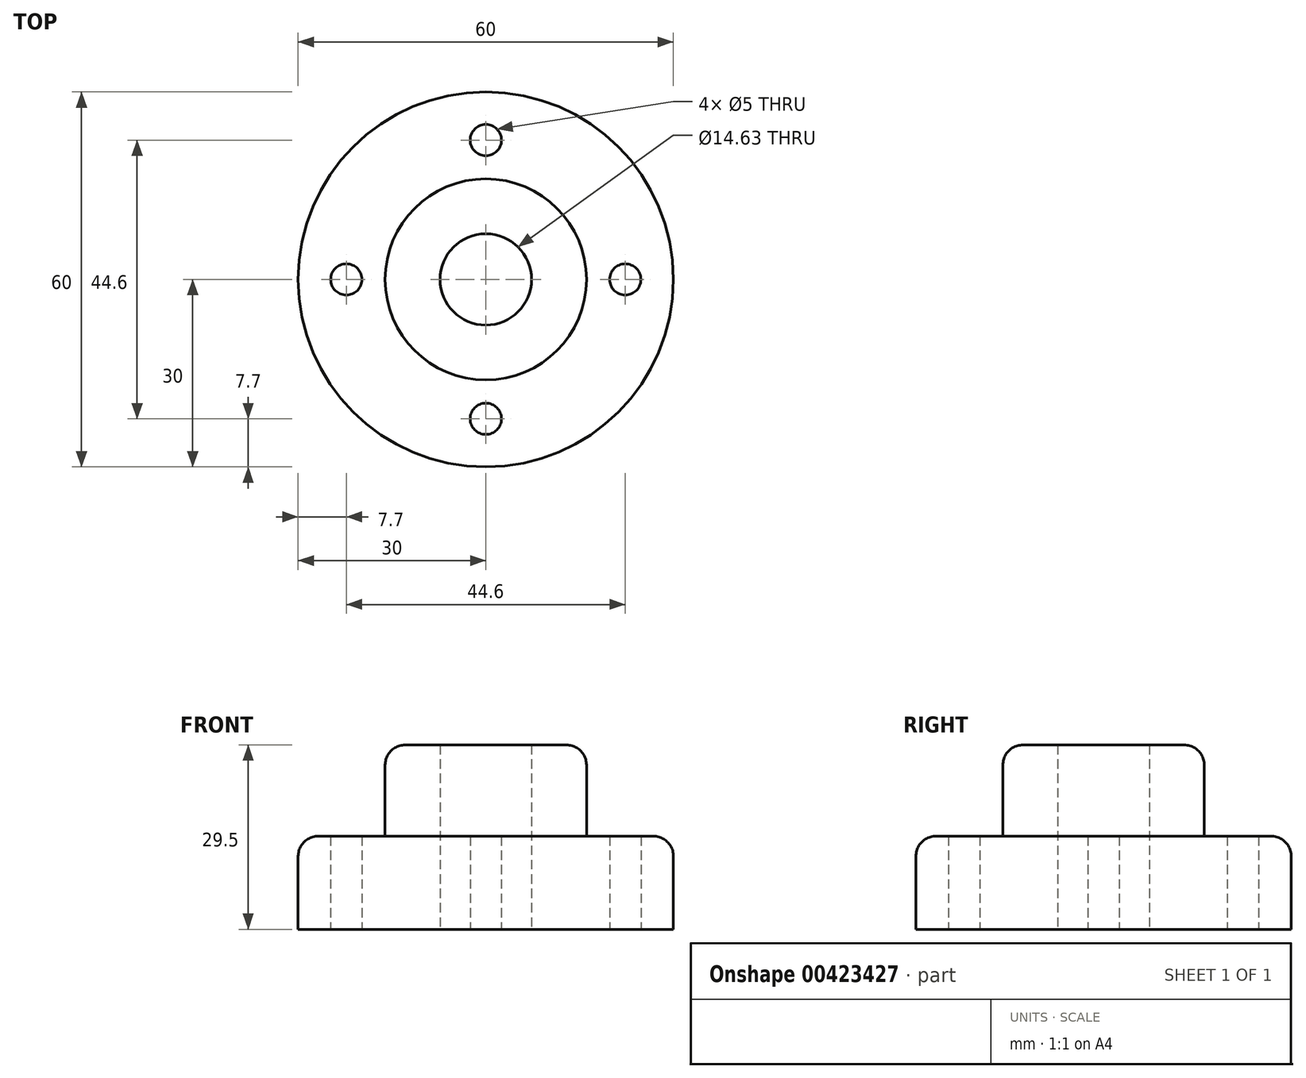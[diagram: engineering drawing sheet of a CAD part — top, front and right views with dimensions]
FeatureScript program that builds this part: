
annotation { "Feature Type Name" : "Feature", "Feature Type Description" : "" }
export const myFeature = defineFeature(function(context is Context, id is Id, definition is map)
    precondition{}
    {
        {
            var Q0;
            Q0=qCreatedBy(makeId("Top.planeOp"),FACE);
            var sketch = newSketch(context, id + "F0", { "sketchPlane" : qUnion([Q0])});
            skCircle(sketch, "E0", {"center": v(0, 0) * mm, "radius": 30 * mm});
            skCircle(sketch, "E1", {"center": v(0, 22.3) * mm, "radius": 2.5 * mm});
            skCircle(sketch, "E2", {"center": v(-22.3, 0) * mm, "radius": 2.5 * mm});
            skCircle(sketch, "E3", {"center": v(0, -22.3) * mm, "radius": 2.5 * mm});
            skCircle(sketch, "E4", {"center": v(22.3, 0) * mm, "radius": 2.5 * mm});
            skSolve(sketch);
        }
        {
            var Q0;
            Q0=makeQuery(id+"F0.imprint","IMPRINT",FACE,{"disambiguationData":[TD([[makeQuery(id+"F0.imprint","IMPRINT",EDGE,{"derivedFrom":sQuery(id+"F0.wireOp",EDGE,"E0")}),1.0]])]});
            var sketch = newSketch(context, id + "F1", { "sketchPlane" : qUnion([Q0])});
            skCircle(sketch, "E5", {"center": v(0, 0) * mm, "radius": 16.1 * mm});
            skCircle(sketch, "E6", {"center": v(0, 0) * mm, "radius": 7.32 * mm});
            skSolve(sketch);
        }
        {
            var Q0;
            Q0 = qSketchRegion(id + "F1", true);
            extrude(context, id + "F2", {"entities" : qUnion([Q0]), "depth" : 14.6 * mm});
        }
        {
            var Q0;
            Q0 = qSketchRegion(id + "F0", true);
            var Q1;
            Q1=makeQuery(id+"F2.opExtrude","CAP_FACE",FACE,{"disambiguationData":[OSD([sQuery(id+"F1.wireOp",EDGE,"E5"),sQuery(id+"F1.wireOp",EDGE,"E6")])],"isStart":false});
            var Q2;
            Q2 = qSketchRegion(id + "F1", true);
            var Q3;
            Q3=makeQuery(id+"F1.imprint","IMPRINT",FACE,{"disambiguationData":[TD([[makeQuery(id+"F1.imprint","IMPRINT",EDGE,{"derivedFrom":sQuery(id+"F1.wireOp",EDGE,"E6")}),1.0]])]});
            extrude(context, id + "F3", {"entities" : qUnion([Q0, Q1, Q2, Q3]), "operationType" : NewBodyOperationType.ADD, "depth" : 14.9 * mm});
        }
        {
            var Q0;
            Q0=makeQuery(id+"F3.opExtrude","CAP_EDGE",EDGE,{"disambiguationData":[OSD([sQuery(id+"F0.wireOp",EDGE,"E0")])],"isStart":false});
            var Q1;
            {var subQ0=sQuery(id+"F1.wireOp",EDGE,"E5");Q1=makeQuery(id+"F3.opExtrude","CAP_EDGE",EDGE,{"disambiguationData":[OSD([subQ0]),TDD([makeQuery(id+"F2.opExtrude","CAP_EDGE",EDGE,{"disambiguationData":[OSD([subQ0])],"isStart":false})])],"isStart":false});}
            fillet(context, id + "F4", {"entities" : qUnion([Q0, Q1]), "radius" : 3.2 * mm, "tangentPropagation" : true, "allowEdgeOverflow" : false});
        }
        {
            var Q0;
            Q0=makeQuery(id+"F3.boolean.opBoolean","SPLIT",FACE,{"disambiguationData":[TD([makeQuery(id+"F3.opExtrude","SWEPT_FACE",FACE,{"disambiguationData":[OSD([sQuery(id+"F1.wireOp",EDGE,"E6")])]})])],"derivedFrom":makeQuery(id+"F3.opExtrude","CAP_FACE",FACE,{"disambiguationData":[OSD([sQuery(id+"F0.wireOp",EDGE,"E0"),sQuery(id+"F0.wireOp",EDGE,"E1"),sQuery(id+"F0.wireOp",EDGE,"E2"),sQuery(id+"F0.wireOp",EDGE,"E3"),sQuery(id+"F0.wireOp",EDGE,"E4")])],"isStart":false})});
            extrude(context, id + "F5", {"entities" : qUnion([Q0]), "operationType" : NewBodyOperationType.REMOVE, "oppositeDirection" : true, "depth" : 25 * mm});
        }
    });
